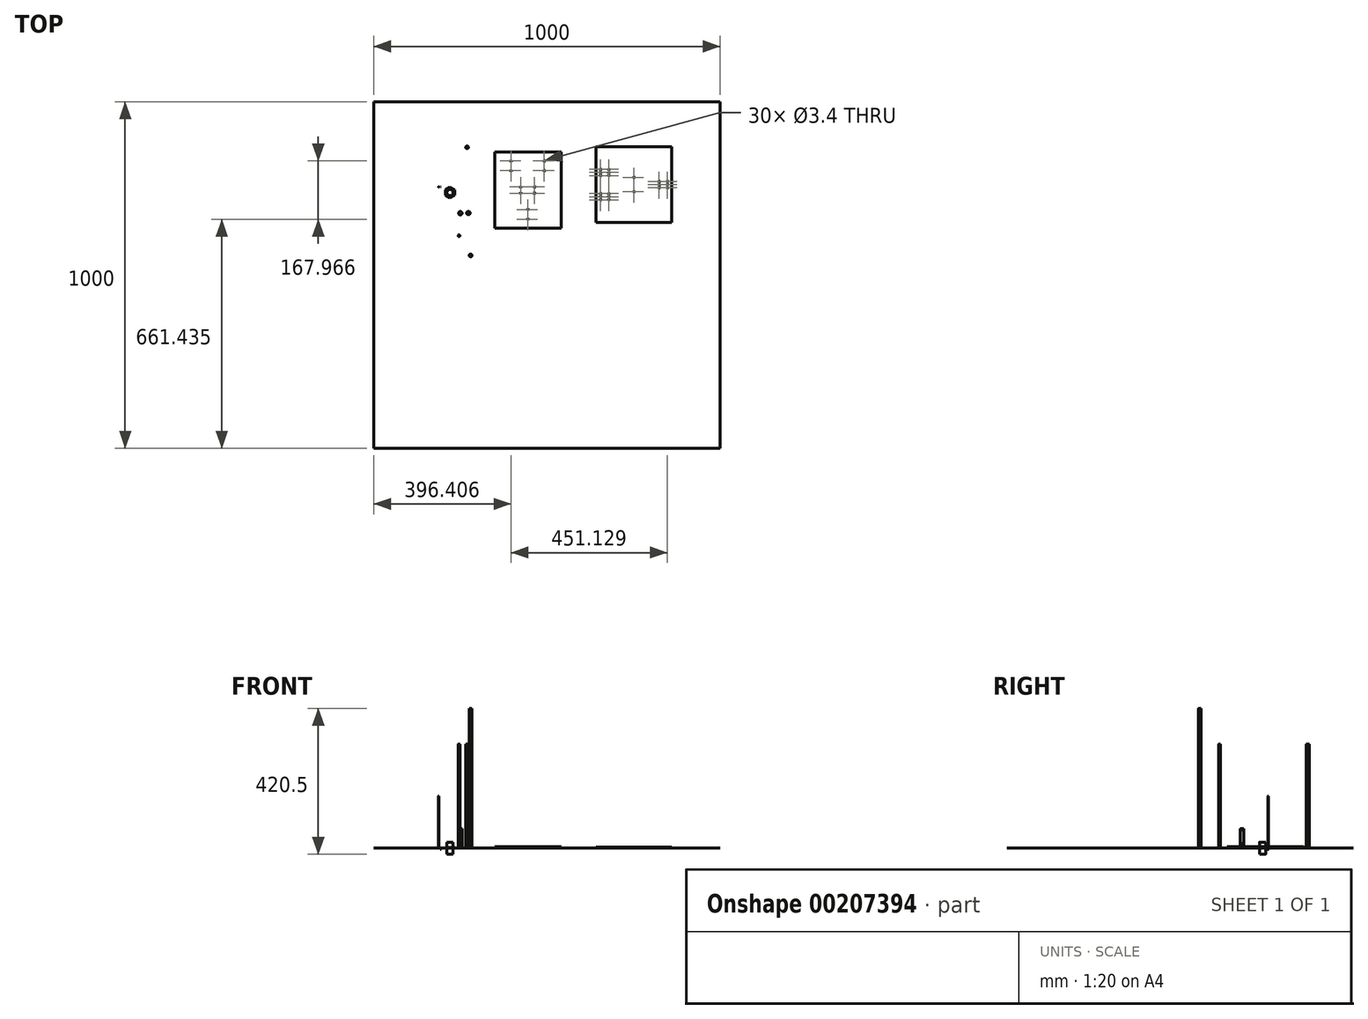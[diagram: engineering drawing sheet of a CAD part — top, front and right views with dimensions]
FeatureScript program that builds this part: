
annotation { "Feature Type Name" : "Feature", "Feature Type Description" : "" }
export const myFeature = defineFeature(function(context is Context, id is Id, definition is map)
    precondition{}
    {
        {
            var Q0;
            Q0=qCreatedBy(makeId("Top.planeOp"),FACE);
            var sketch = newSketch(context, id + "F0", { "sketchPlane" : qUnion([Q0])});
            skLineSegment(sketch, "E0.top", {"start": v(-139.1, -148.1) * mm, "end": v(52.74, -148.1) * mm});
            skLineSegment(sketch, "E0.left", {"start": v(-139.1, 71.9) * mm, "end": v(-139.1, -148.1) * mm});
            skLineSegment(sketch, "E0.right", {"start": v(52.74, 71.9) * mm, "end": v(52.74, -148.1) * mm});
            skCircle(sketch, "E1", {"center": v(-43.18, -122.1) * mm, "radius": 1.7 * mm});
            skCircle(sketch, "E2", {"center": v(-43.18, -94.1) * mm, "radius": 1.7 * mm});
            skPoint(sketch, "E3", {"position": v(-43.18, -148.1) * mm});
            skPoint(sketch, "E4", {"position": v(52.74, -38.1) * mm});
            skPoint(sketch, "E5", {"position": v(-139.1, -38.1) * mm});
            skPoint(sketch, "E6", {"position": v(-44.17, 71.83) * mm});
            skLineSegment(sketch, "E7", {"start": v(-139.1, 71.9) * mm, "end": v(-44.17, 71.83) * mm});
            skLineSegment(sketch, "E8", {"start": v(-44.17, 71.83) * mm, "end": v(52.74, 71.9) * mm});
            skPoint(sketch, "E9", {"position": v(-91.63, 71.86) * mm});
            skPoint(sketch, "E10", {"position": v(4.28, 71.86) * mm});
            skCircle(sketch, "E11", {"center": v(-91.63, 45.86) * mm, "radius": 1.7 * mm});
            skCircle(sketch, "E12", {"center": v(-91.63, 17.86) * mm, "radius": 1.7 * mm});
            skCircle(sketch, "E13", {"center": v(4.28, 45.86) * mm, "radius": 1.7 * mm});
            skCircle(sketch, "E14", {"center": v(4.28, 17.86) * mm, "radius": 1.7 * mm});
            skCircle(sketch, "E15", {"center": v(-23.72, -29.1) * mm, "radius": 1.7 * mm});
            skCircle(sketch, "E16", {"center": v(-23.72, -47.1) * mm, "radius": 1.7 * mm});
            skCircle(sketch, "E17", {"center": v(-63.72, -29.1) * mm, "radius": 1.7 * mm});
            skCircle(sketch, "E18", {"center": v(-63.72, -47.1) * mm, "radius": 1.7 * mm});
            skLineSegment(sketch, "E19", {"start": v(-139.1, -38.1) * mm, "end": v(52.74, -38.1) * mm, "construction": true});
            skLineSegment(sketch, "E20", {"start": v(-44.17, 71.83) * mm, "end": v(-43.18, -148.1) * mm, "construction": true});
            skSolve(sketch);
        }
        {
            var Q0;
            Q0=makeQuery(id+"F0.imprint","IMPRINT",FACE,{"disambiguationData":[TD([[makeQuery(id+"F0.imprint","IMPRINT",EDGE,{"derivedFrom":sQuery(id+"F0.wireOp",EDGE,"E0.top")}),1.0]])]});
            extrude(context, id + "F1", {"entities" : qUnion([Q0]), "depth" : 4 * mm});
        }
        {
            var Q0;
            Q0=qCreatedBy(makeId("Top.planeOp"),FACE);
            var sketch = newSketch(context, id + "F2", { "sketchPlane" : qUnion([Q0])});
            skCircle(sketch, "E21", {"center": v(-218.5, 85.22) * mm, "radius": 4 * mm});
            skCircle(sketch, "E22", {"center": v(-300.48, -29.1) * mm, "radius": 0.88 * mm});
            skSolve(sketch);
        }
        {
            var Q0;
            Q0=makeQuery(id+"F2.imprint","IMPRINT",FACE,{"disambiguationData":[TD([[makeQuery(id+"F2.imprint","IMPRINT",EDGE,{"derivedFrom":sQuery(id+"F2.wireOp",EDGE,"E21")}),1.0]])]});
            extrude(context, id + "F3", {"entities" : qUnion([Q0]), "depth" : 300 * mm, "offsetDistance" : 25 * mm});
        }
        {
            var Q0;
            Q0=qCreatedBy(makeId("Top.planeOp"),FACE);
            var sketch = newSketch(context, id + "F4", { "sketchPlane" : qUnion([Q0])});
            skLineSegment(sketch, "E23.bottom", {"start": v(-488.04, 216.46) * mm, "end": v(511.96, 216.46) * mm});
            skLineSegment(sketch, "E23.top", {"start": v(-488.04, -783.54) * mm, "end": v(511.96, -783.54) * mm});
            skLineSegment(sketch, "E23.left", {"start": v(-488.04, 216.46) * mm, "end": v(-488.04, -783.54) * mm});
            skLineSegment(sketch, "E23.right", {"start": v(511.96, 216.46) * mm, "end": v(511.96, -783.54) * mm});
            skSolve(sketch);
        }
        {
            var Q0;
            Q0=makeQuery(id+"F4.imprint","IMPRINT",FACE,{"disambiguationData":[TD([[makeQuery(id+"F4.imprint","IMPRINT",EDGE,{"derivedFrom":sQuery(id+"F4.wireOp",EDGE,"E23.bottom")}),-1.0]])]});
            extrude(context, id + "F5", {"entities" : qUnion([Q0]), "depth" : 1 * mm});
        }
        {
            var Q0;
            Q0=qCreatedBy(makeId("Top.planeOp"),FACE);
            var sketch = newSketch(context, id + "F6", { "sketchPlane" : qUnion([Q0])});
            skCircle(sketch, "E24", {"center": v(-208.27, -226.5) * mm, "radius": 4 * mm});
            skCircle(sketch, "E25", {"center": v(-241.97, -169.93) * mm, "radius": 2.5 * mm});
            skCircle(sketch, "E26", {"center": v(-267.64, -45.37) * mm, "radius": 9 * mm});
            skCircle(sketch, "E27.cCircle", {"center": v(-267.64, -45.37) * mm, "radius": 13.5 * mm, "construction": true});
            skLineSegment(sketch, "E27.0", {"start": v(-281.14, -53.17) * mm, "end": v(-281.14, -37.58) * mm});
            skLineSegment(sketch, "E27.1", {"start": v(-281.14, -37.58) * mm, "end": v(-267.64, -29.79) * mm});
            skLineSegment(sketch, "E27.2", {"start": v(-267.64, -29.79) * mm, "end": v(-254.14, -37.58) * mm});
            skLineSegment(sketch, "E27.3", {"start": v(-254.14, -37.58) * mm, "end": v(-254.14, -53.17) * mm});
            skLineSegment(sketch, "E27.4", {"start": v(-254.14, -53.17) * mm, "end": v(-267.64, -60.96) * mm});
            skLineSegment(sketch, "E27.5", {"start": v(-267.64, -60.96) * mm, "end": v(-281.14, -53.17) * mm});
            skPoint(sketch, "E27.0.midPoint", {"position": v(-281.14, -45.37) * mm});
            skCircle(sketch, "E28", {"center": v(-238.03, -104.9) * mm, "radius": 5 * mm});
            skCircle(sketch, "E29", {"center": v(-214.79, -104.32) * mm, "radius": 5 * mm});
            skCircle(sketch, "E30", {"center": v(-214.79, -104.32) * mm, "radius": 4 * mm});
            skSolve(sketch);
        }
        {
            var Q0;
            Q0=makeQuery(id+"F6.imprint","IMPRINT",FACE,{"disambiguationData":[TD([[makeQuery(id+"F6.imprint","IMPRINT",EDGE,{"derivedFrom":sQuery(id+"F6.wireOp",EDGE,"E24")}),1.0]])]});
            extrude(context, id + "F7", {"entities" : qUnion([Q0]), "depth" : 403 * mm});
        }
        {
            var Q0;
            Q0=makeQuery(id+"F6.imprint","IMPRINT",FACE,{"disambiguationData":[TD([[makeQuery(id+"F6.imprint","IMPRINT",EDGE,{"derivedFrom":sQuery(id+"F6.wireOp",EDGE,"E25")}),1.0]])]});
            extrude(context, id + "F8", {"entities" : qUnion([Q0]), "depth" : 300 * mm});
        }
        {
            var Q0;
            Q0=makeQuery(id+"F6.imprint","IMPRINT",FACE,{"disambiguationData":[TD([[makeQuery(id+"F6.imprint","IMPRINT",EDGE,{"derivedFrom":sQuery(id+"F6.wireOp",EDGE,"E26")}),1.0]])]});
            extrude(context, id + "F9", {"entities" : qUnion([Q0]), "depth" : (70 / 2) * mm, "symmetric" : true});
        }
        {
            var Q0;
            Q0=makeQuery(id+"F6.imprint","IMPRINT",FACE,{"disambiguationData":[TD([[makeQuery(id+"F6.imprint","IMPRINT",EDGE,{"derivedFrom":sQuery(id+"F6.wireOp",EDGE,"E26")}),-1.0]])]});
            extrude(context, id + "F10", {"entities" : qUnion([Q0]), "operationType" : NewBodyOperationType.ADD, "depth" : 2 * mm});
        }
        {
            var Q0;
            Q0=makeQuery(id+"F6.imprint","IMPRINT",FACE,{"disambiguationData":[TD([[makeQuery(id+"F6.imprint","IMPRINT",EDGE,{"derivedFrom":sQuery(id+"F6.wireOp",EDGE,"E28")}),1.0]])]});
            var Q1;
            Q1=sQuery(id+"F6.wireOp",EDGE,"E28");
            extrude(context, id + "F11", {"entities" : qUnion([Q0]), "surfaceEntities" : qUnion([Q1]), "depth" : 56 * mm});
        }
        {
            var Q0;
            Q0=makeQuery(id+"F6.imprint","IMPRINT",FACE,{"disambiguationData":[TD([[makeQuery(id+"F6.imprint","IMPRINT",EDGE,{"derivedFrom":sQuery(id+"F6.wireOp",EDGE,"E29")}),1.0]])]});
            extrude(context, id + "F12", {"entities" : qUnion([Q0]), "depth" : 52 * mm, "hasSecondDirection" : true, "secondDirectionOppositeDirection" : false, "secondDirectionDepth" : 13 * mm});
        }
        {
            var Q0;
            Q0=makeQuery(id+"F6.imprint","IMPRINT",FACE,{"disambiguationData":[TD([[makeQuery(id+"F6.imprint","IMPRINT",EDGE,{"derivedFrom":sQuery(id+"F6.wireOp",EDGE,"E30")}),1.0]])]});
            extrude(context, id + "F13", {"entities" : qUnion([Q0]), "operationType" : NewBodyOperationType.ADD, "depth" : 52 * mm});
        }
        {
            var Q0;
            Q0=qCreatedBy(makeId("Top.planeOp"),FACE);
            var sketch = newSketch(context, id + "F14", { "sketchPlane" : qUnion([Q0])});
            skLineSegment(sketch, "E31.bottom", {"start": v(153.5, 87.23) * mm, "end": v(372.5, 87.23) * mm});
            skLineSegment(sketch, "E31.top", {"start": v(153.5, -131.77) * mm, "end": v(372.5, -131.77) * mm});
            skLineSegment(sketch, "E31.left", {"start": v(153.5, 87.23) * mm, "end": v(153.5, -131.77) * mm});
            skLineSegment(sketch, "E31.right", {"start": v(372.5, 87.23) * mm, "end": v(372.5, -131.77) * mm});
            skCircle(sketch, "E32", {"center": v(263, -1.77) * mm, "radius": 1.7 * mm});
            skCircle(sketch, "E33", {"center": v(263, -42.77) * mm, "radius": 1.7 * mm});
            skPoint(sketch, "E34", {"position": v(263, 87.23) * mm});
            skLineSegment(sketch, "E35", {"start": v(263, -1.77) * mm, "end": v(263, -42.77) * mm, "construction": true});
            skPoint(sketch, "E36", {"position": v(263, -22.27) * mm});
            skPoint(sketch, "E37", {"position": v(153.5, -22.27) * mm});
            skCircle(sketch, "E38", {"center": v(359.5, -13.27) * mm, "radius": 1.7 * mm});
            skCircle(sketch, "E39", {"center": v(359.5, -31.27) * mm, "radius": 1.7 * mm});
            skCircle(sketch, "E40", {"center": v(359.5, -22.27) * mm, "radius": 1.7 * mm});
            skPoint(sketch, "E40.centerSnap0", {"position": v(372.5, -22.27) * mm});
            skCircle(sketch, "E41", {"center": v(335.5, -22.27) * mm, "radius": 1.7 * mm});
            skCircle(sketch, "E42", {"center": v(335.5, -13.27) * mm, "radius": 1.7 * mm});
            skCircle(sketch, "E43", {"center": v(335.5, -31.27) * mm, "radius": 1.7 * mm});
            skCircle(sketch, "E44", {"center": v(190.5, 21.73) * mm, "radius": 1.7 * mm});
            skCircle(sketch, "E45", {"center": v(190.5, 3.73) * mm, "radius": 1.7 * mm});
            skCircle(sketch, "E46", {"center": v(190.5, 12.73) * mm, "radius": 1.7 * mm});
            skCircle(sketch, "E47", {"center": v(166.5, 12.73) * mm, "radius": 1.7 * mm});
            skCircle(sketch, "E48", {"center": v(166.5, 21.73) * mm, "radius": 1.7 * mm});
            skCircle(sketch, "E49", {"center": v(166.5, 3.73) * mm, "radius": 1.7 * mm});
            skCircle(sketch, "E50", {"center": v(190.5, -48.27) * mm, "radius": 1.7 * mm});
            skCircle(sketch, "E51", {"center": v(190.5, -66.27) * mm, "radius": 1.7 * mm});
            skCircle(sketch, "E52", {"center": v(190.5, -57.27) * mm, "radius": 1.7 * mm});
            skCircle(sketch, "E53", {"center": v(166.5, -57.27) * mm, "radius": 1.7 * mm});
            skCircle(sketch, "E54", {"center": v(166.5, -48.27) * mm, "radius": 1.7 * mm});
            skCircle(sketch, "E55", {"center": v(166.5, -66.27) * mm, "radius": 1.7 * mm});
            skCircle(sketch, "E56", {"center": v(-295.2, -29.1) * mm, "radius": 1.5 * mm});
            skSolve(sketch);
        }
        {
            var Q0;
            Q0=makeQuery(id+"F14.imprint","IMPRINT",FACE,{"disambiguationData":[TD([[makeQuery(id+"F14.imprint","IMPRINT",EDGE,{"derivedFrom":sQuery(id+"F14.wireOp",EDGE,"E31.bottom")}),-1.0]])]});
            extrude(context, id + "F15", {"entities" : qUnion([Q0]), "depth" : 3 * mm});
        }
        {
            var Q0;
            Q0=makeQuery(id+"F2.imprint","IMPRINT",FACE,{"disambiguationData":[TD([[makeQuery(id+"F2.imprint","IMPRINT",EDGE,{"derivedFrom":sQuery(id+"F2.wireOp",EDGE,"E22")}),1.0]])]});
            var Q1;
            Q1=sQuery(id+"F2.wireOp",EDGE,"E22");
            extrude(context, id + "F16", {"entities" : qUnion([Q0]), "surfaceEntities" : qUnion([Q1]), "depth" : 150 * mm, "offsetDistance" : 25 * mm});
        }
        {
            var Q0;
            Q0=makeQuery(id+"F14.imprint","IMPRINT",FACE,{"disambiguationData":[TD([[makeQuery(id+"F14.imprint","IMPRINT",EDGE,{"derivedFrom":sQuery(id+"F14.wireOp",EDGE,"E56")}),1.0]])]});
            var Q1;
            Q1=sQuery(id+"F2.wireOp",EDGE,"E22");
            extrude(context, id + "F17", {"entities" : qUnion([Q0]), "surfaceEntities" : qUnion([Q1]), "oppositeDirection" : true, "depth" : 3 * mm, "offsetDistance" : 25 * mm});
        }
    });
